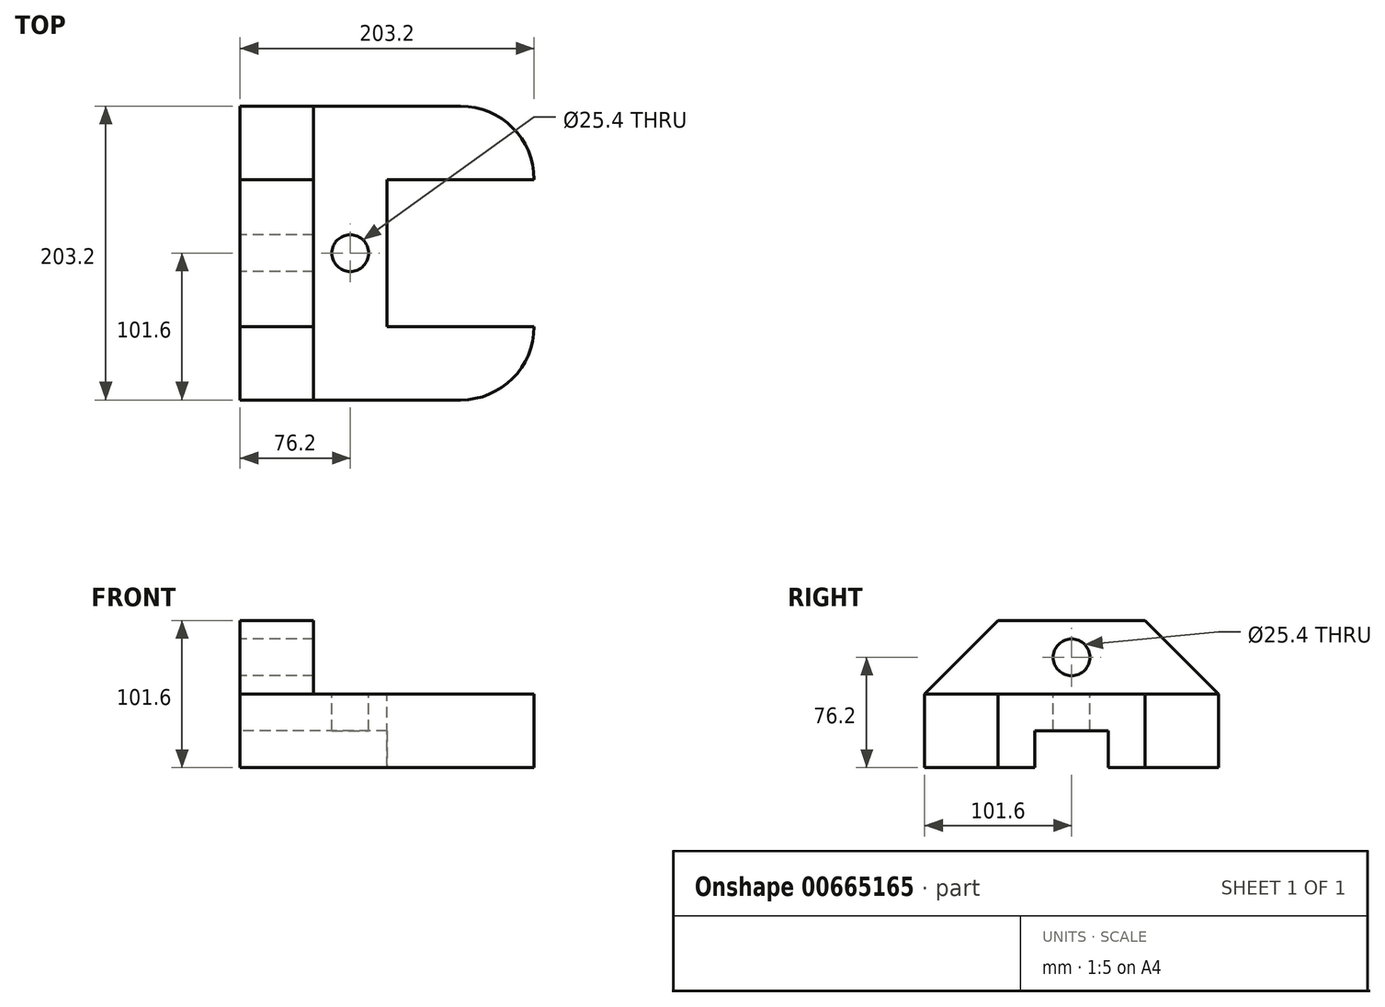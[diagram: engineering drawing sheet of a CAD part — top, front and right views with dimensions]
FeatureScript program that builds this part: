
annotation { "Feature Type Name" : "Feature", "Feature Type Description" : "" }
export const myFeature = defineFeature(function(context is Context, id is Id, definition is map)
    precondition{}
    {
        {
            var Q0;
            Q0=qCreatedBy(makeId("Front.planeOp"),FACE);
            var sketch = newSketch(context, id + "F0", { "sketchPlane" : qUnion([Q0])});
            skLineSegment(sketch, "E0", {"start": v(0, 0) * mm, "end": v(203.2, 0) * mm});
            skLineSegment(sketch, "E1", {"start": v(203.2, 0) * mm, "end": v(203.2, 50.8) * mm});
            skLineSegment(sketch, "E2", {"start": v(203.2, 50.8) * mm, "end": v(50.8, 50.8) * mm});
            skLineSegment(sketch, "E3", {"start": v(50.8, 50.8) * mm, "end": v(50.8, 101.6) * mm});
            skLineSegment(sketch, "E4", {"start": v(50.8, 101.6) * mm, "end": v(0, 101.6) * mm});
            skLineSegment(sketch, "E5", {"start": v(0, 101.6) * mm, "end": v(0, 0) * mm});
            skSolve(sketch);
        }
        {
            var Q0;
            Q0 = qSketchRegion(id + "F0", true);
            extrude(context, id + "F1", {"entities" : qUnion([Q0]), "endBound" : BoundingType.SYMMETRIC, "depth" : 203.2 * mm, "offsetDistance" : 25.4 * mm});
        }
        {
            var Q0;
            Q0=makeQuery(id+"F1.opExtrude","SWEPT_FACE",FACE,{"disambiguationData":[OSD([sQuery(id+"F0.wireOp",EDGE,"E2")])]});
            var sketch = newSketch(context, id + "F2", { "sketchPlane" : qUnion([Q0])});
            skLineSegment(sketch, "E6", {"start": v(203.2, -50.8) * mm, "end": v(101.6, -50.8) * mm});
            skLineSegment(sketch, "E7", {"start": v(101.6, -50.8) * mm, "end": v(101.6, 50.8) * mm});
            skLineSegment(sketch, "E8", {"start": v(101.6, 50.8) * mm, "end": v(203.2, 50.8) * mm});
            skLineSegment(sketch, "E9", {"start": v(203.2, -50.8) * mm, "end": v(203.2, 50.8) * mm});
            skCircle(sketch, "E10", {"center": v(76.2, 0) * mm, "radius": 12.7 * mm});
            skSolve(sketch);
        }
        {
            var Q0;
            Q0=makeQuery(id+"F1.opExtrude","SWEPT_FACE",FACE,{"disambiguationData":[OSD([sQuery(id+"F0.wireOp",EDGE,"E5")])]});
            var sketch = newSketch(context, id + "F3", { "sketchPlane" : qUnion([Q0])});
            skLineSegment(sketch, "E11", {"start": v(-50.8, 101.6) * mm, "end": v(-101.6, 50.8) * mm});
            skLineSegment(sketch, "E12", {"start": v(50.8, 101.6) * mm, "end": v(101.6, 50.8) * mm});
            skCircle(sketch, "E13", {"center": v(0, 76.2) * mm, "radius": 12.7 * mm});
            skLineSegment(sketch, "E14.0", {"start": v(25.4, 25.4) * mm, "end": v(25.4, 0) * mm});
            skLineSegment(sketch, "E15.0", {"start": v(-25.4, 25.4) * mm, "end": v(-25.4, 0) * mm});
            skLineSegment(sketch, "E16", {"start": v(-25.4, 25.4) * mm, "end": v(25.4, 25.4) * mm});
            skSolve(sketch);
        }
        {
            var Q0;
            Q0=makeQuery(id+"F2.imprint","IMPRINT",FACE,{"disambiguationData":[TD([[makeQuery(id+"F2.imprint","IMPRINT",EDGE,{"derivedFrom":sQuery(id+"F2.wireOp",EDGE,"E10")}),1.0]])]});
            var Q1;
            Q1=makeQuery(id+"F2.imprint","IMPRINT",FACE,{"disambiguationData":[TD([[makeQuery(id+"F2.imprint","IMPRINT",EDGE,{"derivedFrom":sQuery(id+"F2.wireOp",EDGE,"E6")}),-1.0]])]});
            extrude(context, id + "F4", {"entities" : qUnion([Q0, Q1]), "operationType" : NewBodyOperationType.REMOVE, "oppositeDirection" : true, "depth" : 50.8 * mm, "offsetDistance" : 25.4 * mm});
        }
        {
            var Q0;
            {var subQ0=sQuery(id+"F3.wireOp",EDGE,"E11");Q0=makeQuery(id+"F3.imprint","IMPRINT",FACE,{"disambiguationData":[TD([[makeQuery(id+"F3.imprint","IMPRINT",EDGE,{"derivedFrom":subQ0}),-1.0]])]});}
            var Q1;
            Q1=makeQuery(id+"F3.imprint","IMPRINT",FACE,{"disambiguationData":[TD([[makeQuery(id+"F3.imprint","IMPRINT",EDGE,{"derivedFrom":sQuery(id+"F3.wireOp",EDGE,"E13")}),1.0]])]});
            var Q2;
            {var subQ0=sQuery(id+"F3.wireOp",EDGE,"E12");Q2=makeQuery(id+"F3.imprint","IMPRINT",FACE,{"disambiguationData":[TD([[makeQuery(id+"F3.imprint","IMPRINT",EDGE,{"derivedFrom":subQ0}),1.0]])]});}
            extrude(context, id + "F5", {"entities" : qUnion([Q0, Q1, Q2]), "operationType" : NewBodyOperationType.REMOVE, "oppositeDirection" : true, "depth" : 50.8 * mm, "offsetDistance" : 25.4 * mm});
        }
        {
            var Q0;
            {var subQ0=sQuery(id+"F3.wireOp",EDGE,"E14.0");Q0=makeQuery(id+"F3.imprint","IMPRINT",FACE,{"disambiguationData":[TD([[makeQuery(id+"F3.imprint","IMPRINT",EDGE,{"derivedFrom":subQ0}),-1.0]])]});}
            extrude(context, id + "F6", {"entities" : qUnion([Q0]), "operationType" : NewBodyOperationType.REMOVE, "oppositeDirection" : true, "depth" : 101.6 * mm, "offsetDistance" : 25.4 * mm});
        }
        {
            var Q0;
            Q0=makeQuery(id+"F1.opExtrude","CAP_EDGE",EDGE,{"disambiguationData":[OSD([sQuery(id+"F0.wireOp",EDGE,"E1")])],"isStart":false});
            var Q1;
            Q1=makeQuery(id+"F1.opExtrude","CAP_EDGE",EDGE,{"disambiguationData":[OSD([sQuery(id+"F0.wireOp",EDGE,"E1")])],"isStart":true});
            fillet(context, id + "F7", {"entities" : qUnion([Q0, Q1]), "radius" : 50.8 * mm, "tangentPropagation" : true, "allowEdgeOverflow" : false});
        }
    });
